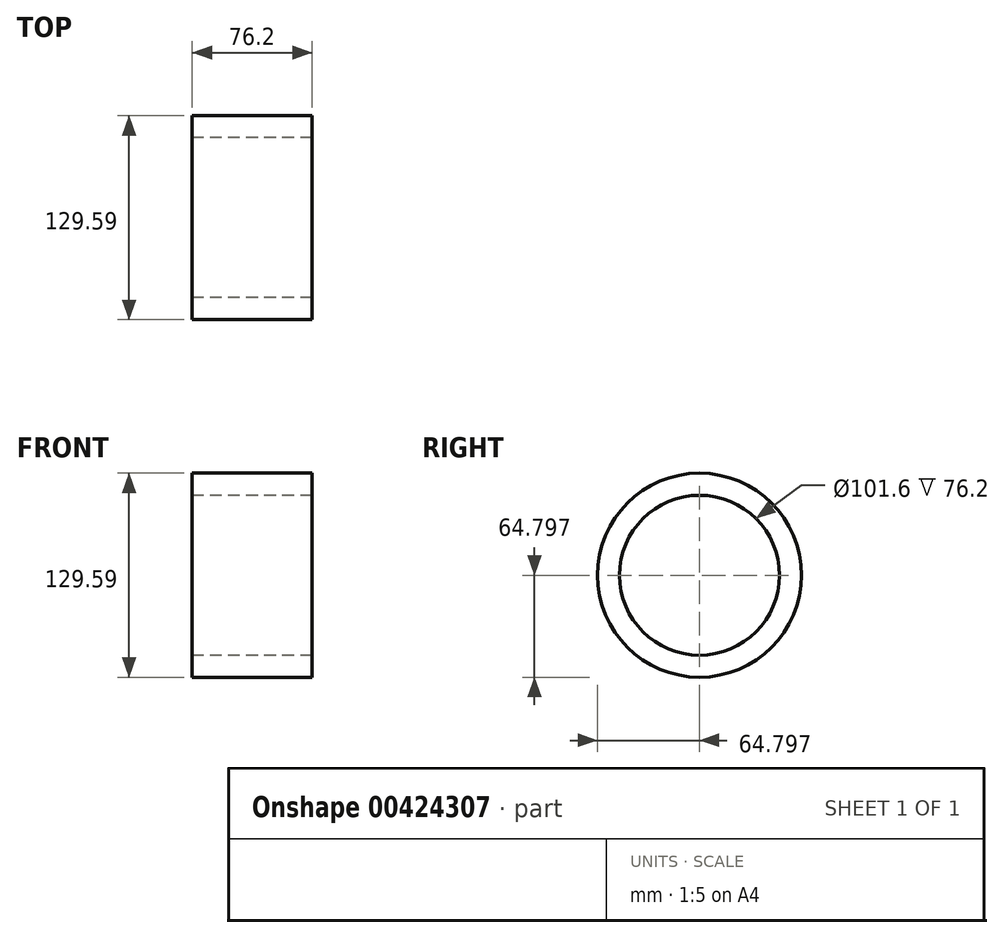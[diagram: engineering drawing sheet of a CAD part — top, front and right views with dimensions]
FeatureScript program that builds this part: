
annotation { "Feature Type Name" : "Feature", "Feature Type Description" : "" }
export const myFeature = defineFeature(function(context is Context, id is Id, definition is map)
    precondition{}
    {
        {
            var Q0;
            Q0=qCreatedBy(makeId("Right.planeOp"),FACE);
            var sketch = newSketch(context, id + "F0", { "sketchPlane" : qUnion([Q0])});
            skCircle(sketch, "E0", {"center": v(-8.1, -10.88) * mm, "radius": 64.8 * mm});
            skPoint(sketch, "E0.first.point", {"position": v(-53.26, 35.59) * mm});
            skPoint(sketch, "E0.second.point", {"position": v(43.23, 28.66) * mm});
            skPoint(sketch, "E0.third.point", {"position": v(25.32, -66.4) * mm});
            skSolve(sketch);
        }
        {
            var Q0;
            Q0=makeQuery(id+"F0.imprint","IMPRINT",FACE,{"disambiguationData":[TD([[makeQuery(id+"F0.imprint","IMPRINT",EDGE,{"derivedFrom":sQuery(id+"F0.wireOp",EDGE,"E0")}),1.0]])]});
            extrude(context, id + "F1", {"entities" : qUnion([Q0]), "depth" : 76.2 * mm});
        }
        {
            var Q0;
            Q0 = qSketchRegion(id + "F0", true);
            extrude(context, id + "F2", {"entities" : qUnion([Q0]), "operationType" : NewBodyOperationType.ADD, "depth" : 25.4 * mm});
        }
        {
            var Q0;
            Q0=sQuery(id+"F0.wireOp",VERTEX,"E0.center");
            var Q1;
            Q1=makeQuery(id+"F1.opExtrude","SWEPT_BODY",BODY,{"disambiguationData":[OSD([sQuery(id+"F0.wireOp",EDGE,"E0")])]});
            hole(context, id + "F3", {"style" : HoleStyle.SIMPLE, "endStyle" : HoleEndStyle.BLIND, "oppositeDirection" : true, "holeDiameter" : 101.6 * mm, "holeDepth" : 127 * mm, "isTappedThrough" : true, "tappedDepth" : 12.7 * mm, "tapClearance" : 3, "startFromSketch" : true, "locations" : qUnion([Q0]), "scope" : qUnion([Q1])});
        }
    });
